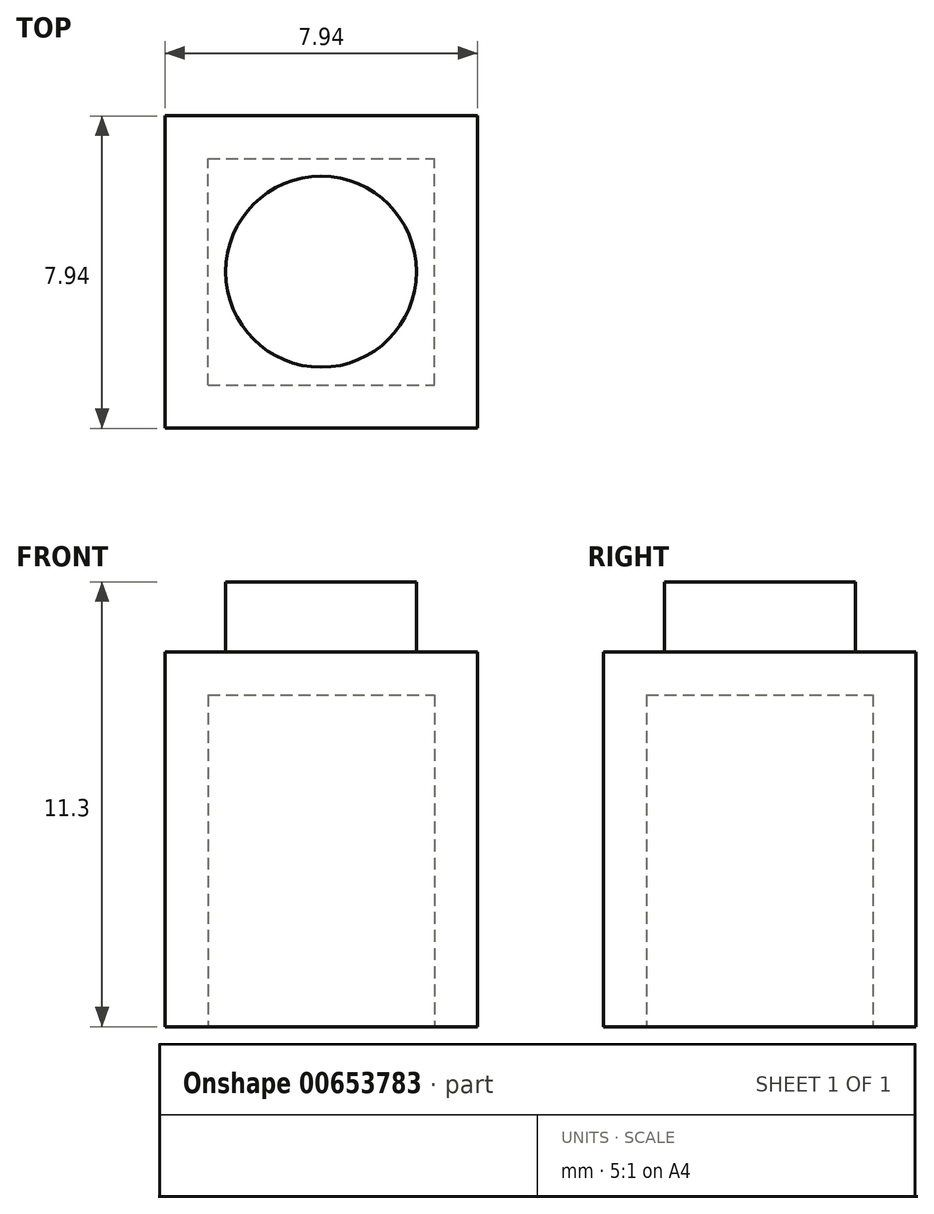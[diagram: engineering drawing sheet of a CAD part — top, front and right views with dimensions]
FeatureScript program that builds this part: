
annotation { "Feature Type Name" : "Feature", "Feature Type Description" : "" }
export const myFeature = defineFeature(function(context is Context, id is Id, definition is map)
    precondition{}
    {
        {
            var Q0;
            Q0=qCreatedBy(makeId("Top.planeOp"),FACE);
            var sketch = newSketch(context, id + "F0", { "sketchPlane" : qUnion([Q0])});
            skLineSegment(sketch, "E0.bottom", {"start": v(-22.76, 15.7) * mm, "end": v(-14.82, 15.7) * mm});
            skLineSegment(sketch, "E0.top", {"start": v(-22.76, 7.76) * mm, "end": v(-14.82, 7.76) * mm});
            skLineSegment(sketch, "E0.left", {"start": v(-22.76, 15.7) * mm, "end": v(-22.76, 7.76) * mm});
            skLineSegment(sketch, "E0.right", {"start": v(-14.82, 15.7) * mm, "end": v(-14.82, 7.76) * mm});
            skSolve(sketch);
        }
        {
            var Q0;
            Q0 = qSketchRegion(id + "F0", true);
            extrude(context, id + "F1", {"entities" : qUnion([Q0]), "depth" : 9.52 * mm, "offsetDistance" : 25.4 * mm});
        }
        {
            var Q0;
            Q0=makeQuery(id+"F1.opExtrude","CAP_FACE",FACE,{"disambiguationData":[OSD([sQuery(id+"F0.wireOp",EDGE,"E0.bottom"),sQuery(id+"F0.wireOp",EDGE,"E0.top"),sQuery(id+"F0.wireOp",EDGE,"E0.left"),sQuery(id+"F0.wireOp",EDGE,"E0.right")])],"isStart":false});
            var sketch = newSketch(context, id + "F2", { "sketchPlane" : qUnion([Q0])});
            skCircle(sketch, "E1", {"center": v(-18.8, 11.74) * mm, "radius": 2.43 * mm});
            skSolve(sketch);
        }
        {
            var Q0;
            Q0 = qSketchRegion(id + "F2", true);
            extrude(context, id + "F3", {"entities" : qUnion([Q0]), "operationType" : NewBodyOperationType.ADD, "depth" : 1.78 * mm, "offsetDistance" : 25.4 * mm});
        }
        {
            var Q0;
            Q0=makeQuery(id+"F1.opExtrude","CAP_FACE",FACE,{"disambiguationData":[OSD([sQuery(id+"F0.wireOp",EDGE,"E0.bottom"),sQuery(id+"F0.wireOp",EDGE,"E0.top"),sQuery(id+"F0.wireOp",EDGE,"E0.left"),sQuery(id+"F0.wireOp",EDGE,"E0.right")])],"isStart":true});
            var sketch = newSketch(context, id + "F4", { "sketchPlane" : qUnion([Q0])});
            skLineSegment(sketch, "E2.bottom", {"start": v(-21.66, -8.86) * mm, "end": v(-15.91, -8.86) * mm});
            skLineSegment(sketch, "E2.top", {"start": v(-21.66, -14.6) * mm, "end": v(-15.91, -14.6) * mm});
            skLineSegment(sketch, "E2.left", {"start": v(-21.66, -8.86) * mm, "end": v(-21.66, -14.6) * mm});
            skLineSegment(sketch, "E2.right", {"start": v(-15.91, -8.86) * mm, "end": v(-15.91, -14.6) * mm});
            skSolve(sketch);
        }
        {
            var Q0;
            Q0 = qSketchRegion(id + "F4", true);
            extrude(context, id + "F5", {"entities" : qUnion([Q0]), "operationType" : NewBodyOperationType.REMOVE, "oppositeDirection" : true, "depth" : 8.43 * mm, "offsetDistance" : 25.4 * mm});
        }
    });
